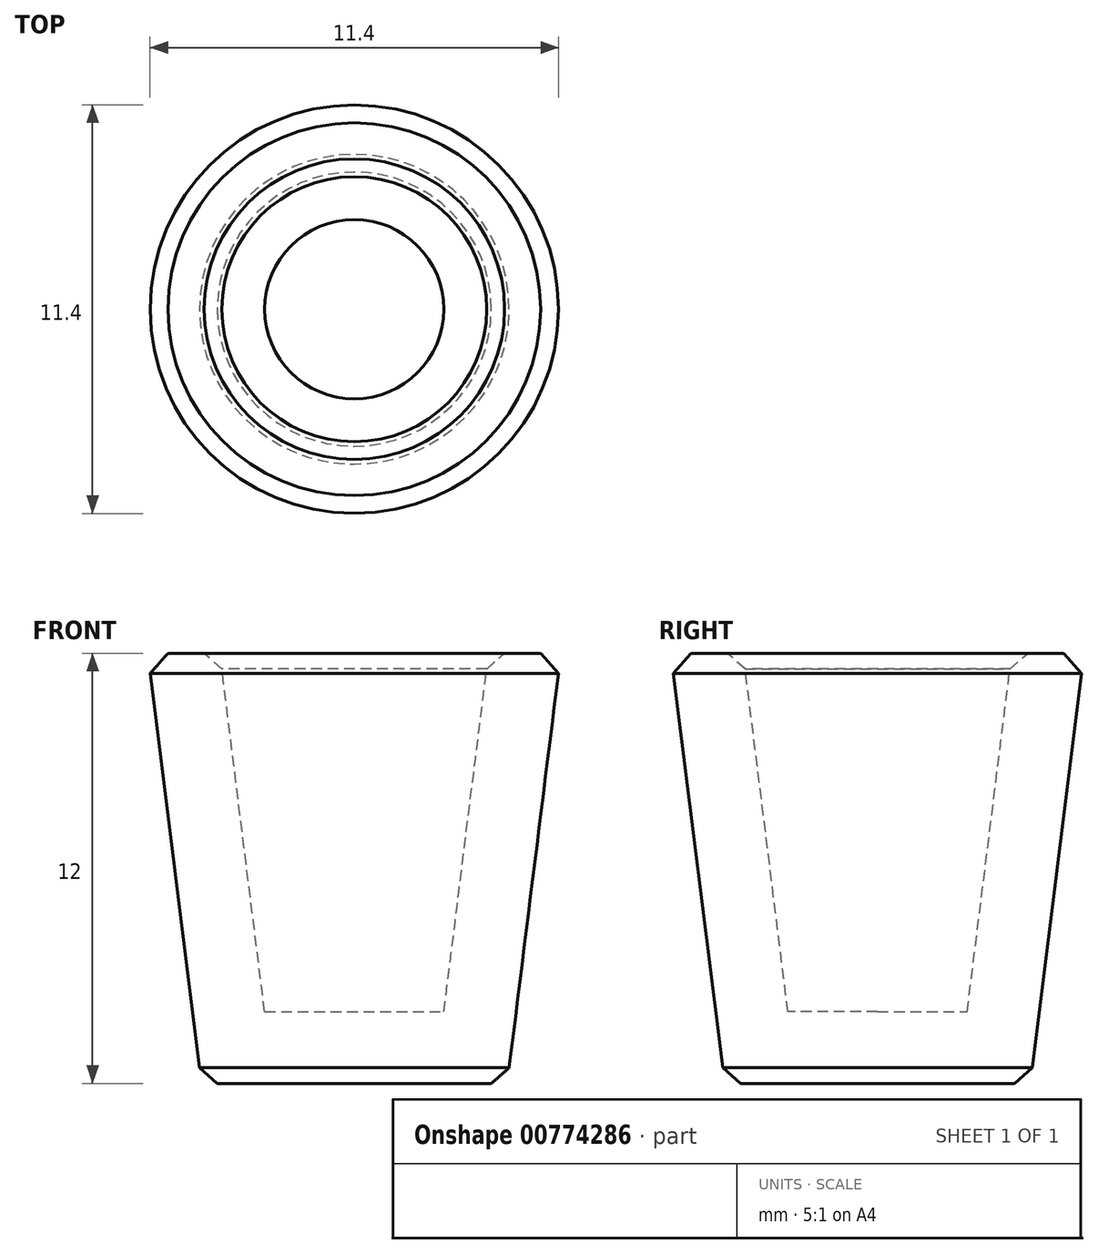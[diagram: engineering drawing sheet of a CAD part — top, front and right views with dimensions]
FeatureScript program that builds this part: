
annotation { "Feature Type Name" : "Feature", "Feature Type Description" : "" }
export const myFeature = defineFeature(function(context is Context, id is Id, definition is map)
    precondition{}
    {
        {
            var Q0;
            Q0=qCreatedBy(makeId("Front.planeOp"),FACE);
            var sketch = newSketch(context, id + "F0", { "sketchPlane" : qUnion([Q0])});
            skLineSegment(sketch, "E0", {"start": v(0, 0) * mm, "end": v(2.5, 0) * mm});
            skLineSegment(sketch, "E1", {"start": v(3.75, 10) * mm, "end": v(2.5, 0) * mm});
            skLineSegment(sketch, "E2.0", {"start": v(0, -2) * mm, "end": v(4.27, -2) * mm});
            skLineSegment(sketch, "E2.1", {"start": v(5.77, 10) * mm, "end": v(4.27, -2) * mm});
            skLineSegment(sketch, "E3", {"start": v(0, -2) * mm, "end": v(0, 0) * mm});
            skLineSegment(sketch, "E4", {"start": v(3.75, 10) * mm, "end": v(5.77, 10) * mm});
            skSolve(sketch);
        }
        {
            var Q0;
            Q0 = qSketchRegion(id + "F0", true);
            var Q1;
            Q1=sQuery(id+"F0.wireOp",EDGE,"E3");
            revolve(context, id + "F1", {"surfaceOperationType" : NewSurfaceOperationType.NEW, "entities" : qUnion([Q0]), "axis" : qUnion([Q1]), "revolveType" : RevolveType.FULL});
        }
        {
            var Q0;
            Q0=makeQuery(id+"F1.opRevolve","SWEPT_EDGE",EDGE,{"disambiguationData":[OSD([sQuery(id+"F0.wireOp",EDGE,"E2.0"),sQuery(id+"F0.wireOp",EDGE,"E2.1")])]});
            var Q1;
            Q1=makeQuery(id+"F1.opRevolve","SWEPT_EDGE",EDGE,{"disambiguationData":[OSD([sQuery(id+"F0.wireOp",EDGE,"E1"),sQuery(id+"F0.wireOp",EDGE,"E4")])]});
            var Q2;
            Q2=makeQuery(id+"F1.opRevolve","SWEPT_EDGE",EDGE,{"disambiguationData":[OSD([sQuery(id+"F0.wireOp",EDGE,"E2.1"),sQuery(id+"F0.wireOp",EDGE,"E4")])]});
            chamfer(context, id + "F2", {"entities" : qUnion([Q0, Q1, Q2]), "width" : .5 * mm, "tangentPropagation" : true});
        }
    });
